# Revit family: RN 90026 Optifitt-Serra-Nippel doppio ridotto
name_source: partatom
category: Rohrformteile
units: mm (PartAtom-declared; Revit-internal decimal feet)

## family parameters
Arbeitsebenenbasiert = Nein
Beim Laden mit Abzugskörper schneiden = Nein
Bemaßung runder Anschluss = Durchmesser verwenden
Gemeinsam genutzt = Nein
Immer vertikal = Ja
Teiletyp = Nicht definiert

## types (14) — shared parameters
1.010.00.2 Blattnummer der Richtlinie = 29
1.010.00.3 Ausgabedatum (Monat) der Richtlinie = 201308
1.010.00.4 Herstellername = R. Nussbaum AG
1.010.00.5 Revisionsdatum der Datei = 20190521
1.010.00.6 Webadresse des Herstellers = http://www.nussbaum.ch
1.100.00.4 Produktbezeichnung = Versorgung
1.110.00.2 Index = 3
1.110.00.4 Produktbezeichnung = Optifitt-Serra
1.960/3L.00.8 Link (URL) = https://www.nussbaum.ch
29.700.00.4 Produktname = Optifitt-Serra-Doppelnippel reduziert
29.700.00.5 Produktkennung = 2
29.700.00.6 Querschnittsform = 1
29.700.00.7 Nennweitensystem = DN
29.700.00.8 Nenndrucksystem = PN
29.710.02.4 Nenndruck = 16
29.710.02.5 max. zul. Überdruck [hPa] = 1600
29.710.02.7 max. zul. Dauer-Betriebsdruck [hPa] = 1600
29.710.02.9 max. zul. Dauer-Betriebstemperatur [°C] = 90
Connector Visibility = Nein
EnclosingSpace Visibility = Nein

## per-type parameters (varying)
- DN=32x20: 1.800.00.3 TGA-Nummer=01900300000000000000000000000000000000000000000016000000000000000025; 1.800.00.4 Kommentarfeld=90026.30, Optifitt-Serra-Doppelnippel reduziert, DN=32x20, L=46, R=1¼; 1.810.00.3 Hersteller-Bestellnummer=90026.30; 1.810.00.4 DATANORM-Nummer=90026.30; 1.810.00.6 GTIN-Nummer=7612945033833; 29.710.02.10 Formstück-Gewicht [kg]=0.172; 29.710.02.3 Benennung=Optifitt-Serra-Doppelnippel reduziert, DN=32x20, L=46, R=1¼; CONNECTOR0_DIAMETER_dX_0r=32 mm; CONNECTOR0_dX_01=19 mm; CONNECTOR0_ref_dX=19 mm; CONNECTOR1_DIAMETER_dX_0r=20 mm; CONNECTOR1_dX_00=31 mm; CONNECTOR1_dX_01=46 mm; CONNECTOR1_ref_dX=31 mm; CONNENCTOR1_ref_dX2=46 mm; R. Nussbaum AG 90026.21 de Visibility=Nein; R. Nussbaum AG 90026.22 de Visibility=Nein; R. Nussbaum AG 90026.23 de Visibility=Nein; R. Nussbaum AG 90026.24 de Visibility=Nein; R. Nussbaum AG 90026.25 de Visibility=Nein; R. Nussbaum AG 90026.26 de Visibility=Nein; R. Nussbaum AG 90026.27 de Visibility=Nein; R. Nussbaum AG 90026.28 de Visibility=Nein; R. Nussbaum AG 90026.29 de Visibility=Nein; R. Nussbaum AG 90026.30 de Visibility=Ja; R. Nussbaum AG 90026.31 de Visibility=Nein; R. Nussbaum AG 90026.32 de Visibility=Nein; R. Nussbaum AG 90026.33 de Visibility=Nein; R. Nussbaum AG 90026.34 de Visibility=Nein
- DN=65x50: 1.800.00.3 TGA-Nummer=01900300000000000000000000000000000000000000000016000000000000000013; 1.800.00.4 Kommentarfeld=90026.34, Optifitt-Serra-Doppelnippel reduziert, DN=65x50, L=70, R=2½; 1.810.00.3 Hersteller-Bestellnummer=90026.34; 1.810.00.4 DATANORM-Nummer=90026.34; 1.810.00.6 GTIN-Nummer=7612945705303; 29.710.02.10 Formstück-Gewicht [kg]=0.631; 29.710.02.3 Benennung=Optifitt-Serra-Doppelnippel reduziert, DN=65x50, L=70, R=2½; CONNECTOR0_DIAMETER_dX_0r=65 mm; CONNECTOR0_dX_01=27 mm; CONNECTOR0_ref_dX=27 mm; CONNECTOR1_DIAMETER_dX_0r=50 mm; CONNECTOR1_dX_00=46 mm; CONNECTOR1_dX_01=70 mm; CONNECTOR1_ref_dX=46 mm; CONNENCTOR1_ref_dX2=70 mm; R. Nussbaum AG 90026.21 de Visibility=Nein; R. Nussbaum AG 90026.22 de Visibility=Nein; R. Nussbaum AG 90026.23 de Visibility=Nein; R. Nussbaum AG 90026.24 de Visibility=Nein; R. Nussbaum AG 90026.25 de Visibility=Nein; R. Nussbaum AG 90026.26 de Visibility=Nein; R. Nussbaum AG 90026.27 de Visibility=Nein; R. Nussbaum AG 90026.28 de Visibility=Nein; R. Nussbaum AG 90026.29 de Visibility=Nein; R. Nussbaum AG 90026.30 de Visibility=Nein; R. Nussbaum AG 90026.31 de Visibility=Nein; R. Nussbaum AG 90026.32 de Visibility=Nein; R. Nussbaum AG 90026.33 de Visibility=Nein; R. Nussbaum AG 90026.34 de Visibility=Ja
- DN=50x40: 1.800.00.3 TGA-Nummer=01900300000000000000000000000000000000000000000016000000000000000012; 1.800.00.4 Kommentarfeld=90026.33, Optifitt-Serra-Doppelnippel reduziert, DN=50x40, L=59, R=2; 1.810.00.3 Hersteller-Bestellnummer=90026.33; 1.810.00.4 DATANORM-Nummer=90026.33; 1.810.00.5 StLB-Nummer=214.557; 1.810.00.6 GTIN-Nummer=7612945033864; 29.710.02.10 Formstück-Gewicht [kg]=0.355; 29.710.02.3 Benennung=Optifitt-Serra-Doppelnippel reduziert, DN=50x40, L=59, R=2; CONNECTOR0_DIAMETER_dX_0r=50 mm; CONNECTOR0_dX_01=24 mm; CONNECTOR0_ref_dX=24 mm; CONNECTOR1_DIAMETER_dX_0r=40 mm; CONNECTOR1_dX_00=40 mm; CONNECTOR1_dX_01=59 mm; CONNECTOR1_ref_dX=40 mm; CONNENCTOR1_ref_dX2=59 mm; Hersteller=R. Nussbaum AG; Modell=90026.33; R. Nussbaum AG 90026.21 de Visibility=Nein; R. Nussbaum AG 90026.22 de Visibility=Nein; R. Nussbaum AG 90026.23 de Visibility=Nein; R. Nussbaum AG 90026.24 de Visibility=Nein; R. Nussbaum AG 90026.25 de Visibility=Nein; R. Nussbaum AG 90026.26 de Visibility=Nein; R. Nussbaum AG 90026.27 de Visibility=Nein; R. Nussbaum AG 90026.28 de Visibility=Nein; R. Nussbaum AG 90026.29 de Visibility=Nein; R. Nussbaum AG 90026.30 de Visibility=Nein; R. Nussbaum AG 90026.31 de Visibility=Nein; R. Nussbaum AG 90026.32 de Visibility=Nein; R. Nussbaum AG 90026.33 de Visibility=Ja; R. Nussbaum AG 90026.34 de Visibility=Nein; Typenkommentare=Optifitt-Serra-Nippel doppio ridotto DN=50x40; URL=https://www.nussbaum.ch
- DN=50x32: 1.800.00.3 TGA-Nummer=01900300000000000000000000000000000000000000000016000000000000000011; 1.800.00.4 Kommentarfeld=90026.32, Optifitt-Serra-Doppelnippel reduziert, DN=50x32, L=59, R=2; 1.810.00.3 Hersteller-Bestellnummer=90026.32; 1.810.00.4 DATANORM-Nummer=90026.32; 1.810.00.6 GTIN-Nummer=7612945033857; 29.710.02.10 Formstück-Gewicht [kg]=0.363; 29.710.02.3 Benennung=Optifitt-Serra-Doppelnippel reduziert, DN=50x32, L=59, R=2; CONNECTOR0_DIAMETER_dX_0r=50 mm; CONNECTOR0_dX_01=24 mm; CONNECTOR0_ref_dX=24 mm; CONNECTOR1_DIAMETER_dX_0r=32 mm; CONNECTOR1_dX_00=39 mm; CONNECTOR1_dX_01=58 mm; CONNECTOR1_ref_dX=39 mm; CONNENCTOR1_ref_dX2=58 mm; Hersteller=R. Nussbaum AG; Modell=90026.32; R. Nussbaum AG 90026.21 de Visibility=Nein; R. Nussbaum AG 90026.22 de Visibility=Nein; R. Nussbaum AG 90026.23 de Visibility=Nein; R. Nussbaum AG 90026.24 de Visibility=Nein; R. Nussbaum AG 90026.25 de Visibility=Nein; R. Nussbaum AG 90026.26 de Visibility=Nein; R. Nussbaum AG 90026.27 de Visibility=Nein; R. Nussbaum AG 90026.28 de Visibility=Nein; R. Nussbaum AG 90026.29 de Visibility=Nein; R. Nussbaum AG 90026.30 de Visibility=Nein; R. Nussbaum AG 90026.31 de Visibility=Nein; R. Nussbaum AG 90026.32 de Visibility=Ja; R. Nussbaum AG 90026.33 de Visibility=Nein; R. Nussbaum AG 90026.34 de Visibility=Nein; Typenkommentare=Optifitt-Serra-Nippel doppio ridotto DN=50x32; URL=https://www.nussbaum.ch
- DN=40x25: 1.800.00.3 TGA-Nummer=01900300000000000000000000000000000000000000000016000000000000000010; 1.800.00.4 Kommentarfeld=90026.31, Optifitt-Serra-Doppelnippel reduziert, DN=40x25, L=52, R=1½; 1.810.00.3 Hersteller-Bestellnummer=90026.31; 1.810.00.4 DATANORM-Nummer=90026.31; 1.810.00.6 GTIN-Nummer=7612945033840; 29.710.02.10 Formstück-Gewicht [kg]=0.226; 29.710.02.3 Benennung=Optifitt-Serra-Doppelnippel reduziert, DN=40x25, L=52, R=1½; CONNECTOR0_DIAMETER_dX_0r=40 mm; CONNECTOR0_dX_01=19 mm; CONNECTOR0_ref_dX=19 mm; CONNECTOR1_DIAMETER_dX_0r=25 mm  [stored 0.082021 ft]; CONNECTOR1_dX_00=35 mm; CONNECTOR1_dX_01=52 mm; CONNECTOR1_ref_dX=35 mm; CONNENCTOR1_ref_dX2=52 mm; Hersteller=R. Nussbaum AG; Modell=90026.31; R. Nussbaum AG 90026.21 de Visibility=Nein; R. Nussbaum AG 90026.22 de Visibility=Nein; R. Nussbaum AG 90026.23 de Visibility=Nein; R. Nussbaum AG 90026.24 de Visibility=Nein; R. Nussbaum AG 90026.25 de Visibility=Nein; R. Nussbaum AG 90026.26 de Visibility=Nein; R. Nussbaum AG 90026.27 de Visibility=Nein; R. Nussbaum AG 90026.28 de Visibility=Nein; R. Nussbaum AG 90026.29 de Visibility=Nein; R. Nussbaum AG 90026.30 de Visibility=Nein; R. Nussbaum AG 90026.31 de Visibility=Ja; R. Nussbaum AG 90026.32 de Visibility=Nein; R. Nussbaum AG 90026.33 de Visibility=Nein; R. Nussbaum AG 90026.34 de Visibility=Nein; Typenkommentare=Optifitt-Serra-Nippel doppio ridotto DN=40x25; URL=https://www.nussbaum.ch
- DN=25x15: 1.800.00.3 TGA-Nummer=01900300000000000000000000000000000000000000000016000000000000000009; 1.800.00.4 Kommentarfeld=90026.29, Optifitt-Serra-Doppelnippel reduziert, DN=25x15, L=40, R=1; 1.810.00.3 Hersteller-Bestellnummer=90026.29; 1.810.00.4 DATANORM-Nummer=90026.29; 1.810.00.6 GTIN-Nummer=7612945033826; 29.710.02.10 Formstück-Gewicht [kg]=0.089; 29.710.02.3 Benennung=Optifitt-Serra-Doppelnippel reduziert, DN=25x15, L=40, R=1; CONNECTOR0_DIAMETER_dX_0r=25 mm  [stored 0.082021 ft]; CONNECTOR0_dX_01=17 mm; CONNECTOR0_ref_dX=17 mm; CONNECTOR1_DIAMETER_dX_0r=15 mm; CONNECTOR1_dX_00=27 mm; CONNECTOR1_dX_01=40 mm; CONNECTOR1_ref_dX=27 mm; CONNENCTOR1_ref_dX2=40 mm; Hersteller=R. Nussbaum AG; Modell=90026.29; R. Nussbaum AG 90026.21 de Visibility=Nein; R. Nussbaum AG 90026.22 de Visibility=Nein; R. Nussbaum AG 90026.23 de Visibility=Nein; R. Nussbaum AG 90026.24 de Visibility=Nein; R. Nussbaum AG 90026.25 de Visibility=Nein; R. Nussbaum AG 90026.26 de Visibility=Nein; R. Nussbaum AG 90026.27 de Visibility=Nein; R. Nussbaum AG 90026.28 de Visibility=Nein; R. Nussbaum AG 90026.29 de Visibility=Ja; R. Nussbaum AG 90026.30 de Visibility=Nein; R. Nussbaum AG 90026.31 de Visibility=Nein; R. Nussbaum AG 90026.32 de Visibility=Nein; R. Nussbaum AG 90026.33 de Visibility=Nein; R. Nussbaum AG 90026.34 de Visibility=Nein; Typenkommentare=Optifitt-Serra-Nippel doppio ridotto DN=25x15; URL=https://www.nussbaum.ch
- DN=20x12: 1.800.00.3 TGA-Nummer=01900300000000000000000000000000000000000000000016000000000000000008; 1.800.00.4 Kommentarfeld=90026.28, Optifitt-Serra-Doppelnippel reduziert, DN=20x12, L=34, R=¾; 1.810.00.3 Hersteller-Bestellnummer=90026.28; 1.810.00.4 DATANORM-Nummer=90026.28; 1.810.00.6 GTIN-Nummer=7612945033819; 29.710.02.10 Formstück-Gewicht [kg]=0.055; 29.710.02.3 Benennung=Optifitt-Serra-Doppelnippel reduziert, DN=20x12, L=34, R=¾; CONNECTOR0_DIAMETER_dX_0r=20 mm; CONNECTOR0_dX_01=15 mm; CONNECTOR0_ref_dX=15 mm; CONNECTOR1_DIAMETER_dX_0r=12 mm  [stored 0.0393701 ft]; CONNECTOR1_dX_00=24 mm; CONNECTOR1_dX_01=34 mm; CONNECTOR1_ref_dX=24 mm; CONNENCTOR1_ref_dX2=34 mm; Hersteller=R. Nussbaum AG; Modell=90026.28; R. Nussbaum AG 90026.21 de Visibility=Nein; R. Nussbaum AG 90026.22 de Visibility=Nein; R. Nussbaum AG 90026.23 de Visibility=Nein; R. Nussbaum AG 90026.24 de Visibility=Nein; R. Nussbaum AG 90026.25 de Visibility=Nein; R. Nussbaum AG 90026.26 de Visibility=Nein; R. Nussbaum AG 90026.27 de Visibility=Nein; R. Nussbaum AG 90026.28 de Visibility=Ja; R. Nussbaum AG 90026.29 de Visibility=Nein; R. Nussbaum AG 90026.30 de Visibility=Nein; R. Nussbaum AG 90026.31 de Visibility=Nein; R. Nussbaum AG 90026.32 de Visibility=Nein; R. Nussbaum AG 90026.33 de Visibility=Nein; R. Nussbaum AG 90026.34 de Visibility=Nein; Typenkommentare=Optifitt-Serra-Nippel doppio ridotto DN=20x12; URL=https://www.nussbaum.ch
- DN=15x10: 1.800.00.3 TGA-Nummer=01900300000000000000000000000000000000000000000016000000000000000007; 1.800.00.4 Kommentarfeld=90026.27, Optifitt-Serra-Doppelnippel reduziert, DN=15x10, L=31, R=½; 1.810.00.3 Hersteller-Bestellnummer=90026.27; 1.810.00.4 DATANORM-Nummer=90026.27; 1.810.00.6 GTIN-Nummer=7612945033802; 29.710.02.10 Formstück-Gewicht [kg]=0.035; 29.710.02.3 Benennung=Optifitt-Serra-Doppelnippel reduziert, DN=15x10, L=31, R=½; CONNECTOR0_DIAMETER_dX_0r=15 mm; CONNECTOR0_dX_01=13 mm; CONNECTOR0_ref_dX=13 mm; CONNECTOR1_DIAMETER_dX_0r=10 mm  [stored 0.0328084 ft]; CONNECTOR1_dX_00=21 mm; CONNECTOR1_dX_01=31 mm; CONNECTOR1_ref_dX=21 mm; CONNENCTOR1_ref_dX2=31 mm; Hersteller=R. Nussbaum AG; Modell=90026.27; R. Nussbaum AG 90026.21 de Visibility=Nein; R. Nussbaum AG 90026.22 de Visibility=Nein; R. Nussbaum AG 90026.23 de Visibility=Nein; R. Nussbaum AG 90026.24 de Visibility=Nein; R. Nussbaum AG 90026.25 de Visibility=Nein; R. Nussbaum AG 90026.26 de Visibility=Nein; R. Nussbaum AG 90026.27 de Visibility=Ja; R. Nussbaum AG 90026.28 de Visibility=Nein; R. Nussbaum AG 90026.29 de Visibility=Nein; R. Nussbaum AG 90026.30 de Visibility=Nein; R. Nussbaum AG 90026.31 de Visibility=Nein; R. Nussbaum AG 90026.32 de Visibility=Nein; R. Nussbaum AG 90026.33 de Visibility=Nein; R. Nussbaum AG 90026.34 de Visibility=Nein; Typenkommentare=Optifitt-Serra-Nippel doppio ridotto DN=15x10; URL=https://www.nussbaum.ch
- DN=40x32: 1.800.00.3 TGA-Nummer=01900300000000000000000000000000000000000000000016000000000000000006; 1.800.00.4 Kommentarfeld=90026.26, Optifitt-Serra-Doppelnippel reduziert, DN=40x32, L=53, R=1½; 1.810.00.3 Hersteller-Bestellnummer=90026.26; 1.810.00.4 DATANORM-Nummer=90026.26; 1.810.00.5 StLB-Nummer=214.556; 1.810.00.6 GTIN-Nummer=7612945033796; 29.710.02.10 Formstück-Gewicht [kg]=0.226; 29.710.02.3 Benennung=Optifitt-Serra-Doppelnippel reduziert, DN=40x32, L=53, R=1½; CONNECTOR0_DIAMETER_dX_0r=40 mm; CONNECTOR0_dX_01=19 mm; CONNECTOR0_ref_dX=19 mm; CONNECTOR1_DIAMETER_dX_0r=32 mm; CONNECTOR1_dX_00=35 mm; CONNECTOR1_dX_01=54 mm; CONNECTOR1_ref_dX=35 mm; CONNENCTOR1_ref_dX2=54 mm; Hersteller=R. Nussbaum AG; Modell=90026.26; R. Nussbaum AG 90026.21 de Visibility=Nein; R. Nussbaum AG 90026.22 de Visibility=Nein; R. Nussbaum AG 90026.23 de Visibility=Nein; R. Nussbaum AG 90026.24 de Visibility=Nein; R. Nussbaum AG 90026.25 de Visibility=Nein; R. Nussbaum AG 90026.26 de Visibility=Ja; R. Nussbaum AG 90026.27 de Visibility=Nein; R. Nussbaum AG 90026.28 de Visibility=Nein; R. Nussbaum AG 90026.29 de Visibility=Nein; R. Nussbaum AG 90026.30 de Visibility=Nein; R. Nussbaum AG 90026.31 de Visibility=Nein; R. Nussbaum AG 90026.32 de Visibility=Nein; R. Nussbaum AG 90026.33 de Visibility=Nein; R. Nussbaum AG 90026.34 de Visibility=Nein; Typenkommentare=Optifitt-Serra-Nippel doppio ridotto DN=40x32; URL=https://www.nussbaum.ch
- DN=32x25: 1.800.00.3 TGA-Nummer=01900300000000000000000000000000000000000000000016000000000000000005; 1.800.00.4 Kommentarfeld=90026.25, Optifitt-Serra-Doppelnippel reduziert, DN=32x25, L=49, R=1¼; 1.810.00.3 Hersteller-Bestellnummer=90026.25; 1.810.00.4 DATANORM-Nummer=90026.25; 1.810.00.5 StLB-Nummer=214.555; 1.810.00.6 GTIN-Nummer=7612945033789; 29.710.02.10 Formstück-Gewicht [kg]=0.161; 29.710.02.3 Benennung=Optifitt-Serra-Doppelnippel reduziert, DN=32x25, L=49, R=1¼; CONNECTOR0_DIAMETER_dX_0r=32 mm; CONNECTOR0_dX_01=19 mm; CONNECTOR0_ref_dX=19 mm; CONNECTOR1_DIAMETER_dX_0r=25 mm  [stored 0.082021 ft]; CONNECTOR1_dX_00=32 mm; CONNECTOR1_dX_01=49 mm; CONNECTOR1_ref_dX=32 mm; CONNENCTOR1_ref_dX2=49 mm; R. Nussbaum AG 90026.21 de Visibility=Nein; R. Nussbaum AG 90026.22 de Visibility=Nein; R. Nussbaum AG 90026.23 de Visibility=Nein; R. Nussbaum AG 90026.24 de Visibility=Nein; R. Nussbaum AG 90026.25 de Visibility=Ja; R. Nussbaum AG 90026.26 de Visibility=Nein; R. Nussbaum AG 90026.27 de Visibility=Nein; R. Nussbaum AG 90026.28 de Visibility=Nein; R. Nussbaum AG 90026.29 de Visibility=Nein; R. Nussbaum AG 90026.30 de Visibility=Nein; R. Nussbaum AG 90026.31 de Visibility=Nein; R. Nussbaum AG 90026.32 de Visibility=Nein; R. Nussbaum AG 90026.33 de Visibility=Nein; R. Nussbaum AG 90026.34 de Visibility=Nein
- DN=25x20: 1.800.00.3 TGA-Nummer=01900300000000000000000000000000000000000000000016000000000000000004; 1.800.00.4 Kommentarfeld=90026.24, Optifitt-Serra-Doppelnippel reduziert, DN=25x20, L=42, R=1; 1.810.00.3 Hersteller-Bestellnummer=90026.24; 1.810.00.4 DATANORM-Nummer=90026.24; 1.810.00.5 StLB-Nummer=214.554; 1.810.00.6 GTIN-Nummer=7612945033772; 29.710.02.10 Formstück-Gewicht [kg]=0.094; 29.710.02.3 Benennung=Optifitt-Serra-Doppelnippel reduziert, DN=25x20, L=42, R=1; CONNECTOR0_DIAMETER_dX_0r=25 mm  [stored 0.082021 ft]; CONNECTOR0_dX_01=17 mm; CONNECTOR0_ref_dX=17 mm; CONNECTOR1_DIAMETER_dX_0r=20 mm; CONNECTOR1_dX_00=27 mm; CONNECTOR1_dX_01=42 mm; CONNECTOR1_ref_dX=27 mm; CONNENCTOR1_ref_dX2=42 mm; Hersteller=R. Nussbaum AG; Modell=90026.24; R. Nussbaum AG 90026.21 de Visibility=Nein; R. Nussbaum AG 90026.22 de Visibility=Nein; R. Nussbaum AG 90026.23 de Visibility=Nein; R. Nussbaum AG 90026.24 de Visibility=Ja; R. Nussbaum AG 90026.25 de Visibility=Nein; R. Nussbaum AG 90026.26 de Visibility=Nein; R. Nussbaum AG 90026.27 de Visibility=Nein; R. Nussbaum AG 90026.28 de Visibility=Nein; R. Nussbaum AG 90026.29 de Visibility=Nein; R. Nussbaum AG 90026.30 de Visibility=Nein; R. Nussbaum AG 90026.31 de Visibility=Nein; R. Nussbaum AG 90026.32 de Visibility=Nein; R. Nussbaum AG 90026.33 de Visibility=Nein; R. Nussbaum AG 90026.34 de Visibility=Nein; Typenkommentare=Optifitt-Serra-Nippel doppio ridotto DN=25x20; URL=https://www.nussbaum.ch
- DN=20x15: 1.800.00.3 TGA-Nummer=01900300000000000000000000000000000000000000000016000000000000000003; 1.800.00.4 Kommentarfeld=90026.23, Optifitt-Serra-Doppelnippel reduziert, DN=20x15, L=37, R=¾; 1.810.00.3 Hersteller-Bestellnummer=90026.23; 1.810.00.4 DATANORM-Nummer=90026.23; 1.810.00.5 StLB-Nummer=214.553; 1.810.00.6 GTIN-Nummer=7612945033765; 29.710.02.10 Formstück-Gewicht [kg]=0.063; 29.710.02.3 Benennung=Optifitt-Serra-Doppelnippel reduziert, DN=20x15, L=37, R=¾; CONNECTOR0_DIAMETER_dX_0r=20 mm; CONNECTOR0_dX_01=15 mm; CONNECTOR0_ref_dX=15 mm; CONNECTOR1_DIAMETER_dX_0r=15 mm; CONNECTOR1_dX_00=24 mm; CONNECTOR1_dX_01=37 mm; CONNECTOR1_ref_dX=24 mm; CONNENCTOR1_ref_dX2=37 mm; Hersteller=R. Nussbaum AG; Modell=90026.23; R. Nussbaum AG 90026.21 de Visibility=Nein; R. Nussbaum AG 90026.22 de Visibility=Nein; R. Nussbaum AG 90026.23 de Visibility=Ja; R. Nussbaum AG 90026.24 de Visibility=Nein; R. Nussbaum AG 90026.25 de Visibility=Nein; R. Nussbaum AG 90026.26 de Visibility=Nein; R. Nussbaum AG 90026.27 de Visibility=Nein; R. Nussbaum AG 90026.28 de Visibility=Nein; R. Nussbaum AG 90026.29 de Visibility=Nein; R. Nussbaum AG 90026.30 de Visibility=Nein; R. Nussbaum AG 90026.31 de Visibility=Nein; R. Nussbaum AG 90026.32 de Visibility=Nein; R. Nussbaum AG 90026.33 de Visibility=Nein; R. Nussbaum AG 90026.34 de Visibility=Nein; Typenkommentare=Optifitt-Serra-Nippel doppio ridotto DN=20x15; URL=https://www.nussbaum.ch
- DN=15x12: 1.800.00.3 TGA-Nummer=01900300000000000000000000000000000000000000000016000000000000000002; 1.800.00.4 Kommentarfeld=90026.22, Optifitt-Serra-Doppelnippel reduziert, DN=15x12, L=32, R=½; 1.810.00.3 Hersteller-Bestellnummer=90026.22; 1.810.00.4 DATANORM-Nummer=90026.22; 1.810.00.5 StLB-Nummer=214.552; 1.810.00.6 GTIN-Nummer=7612945033758; 29.710.02.10 Formstück-Gewicht [kg]=0.039; 29.710.02.3 Benennung=Optifitt-Serra-Doppelnippel reduziert, DN=15x12, L=32, R=½; CONNECTOR0_DIAMETER_dX_0r=15 mm; CONNECTOR0_dX_01=13 mm; CONNECTOR0_ref_dX=13 mm; CONNECTOR1_DIAMETER_dX_0r=12 mm  [stored 0.0393701 ft]; CONNECTOR1_dX_00=22 mm; CONNECTOR1_dX_01=32 mm; CONNECTOR1_ref_dX=22 mm; CONNENCTOR1_ref_dX2=32 mm; Hersteller=R. Nussbaum AG; Modell=90026.22; R. Nussbaum AG 90026.21 de Visibility=Nein; R. Nussbaum AG 90026.22 de Visibility=Ja; R. Nussbaum AG 90026.23 de Visibility=Nein; R. Nussbaum AG 90026.24 de Visibility=Nein; R. Nussbaum AG 90026.25 de Visibility=Nein; R. Nussbaum AG 90026.26 de Visibility=Nein; R. Nussbaum AG 90026.27 de Visibility=Nein; R. Nussbaum AG 90026.28 de Visibility=Nein; R. Nussbaum AG 90026.29 de Visibility=Nein; R. Nussbaum AG 90026.30 de Visibility=Nein; R. Nussbaum AG 90026.31 de Visibility=Nein; R. Nussbaum AG 90026.32 de Visibility=Nein; R. Nussbaum AG 90026.33 de Visibility=Nein; R. Nussbaum AG 90026.34 de Visibility=Nein; Typenkommentare=Optifitt-Serra-Nippel doppio ridotto DN=15x12; URL=https://www.nussbaum.ch
- DN=12x10: 1.800.00.3 TGA-Nummer=01900300000000000000000000000000000000000000000016000000000000000001; 1.800.00.4 Kommentarfeld=90026.21, Optifitt-Serra-Doppelnippel reduziert, DN=12x10, L=28, R=3/8; 1.810.00.3 Hersteller-Bestellnummer=90026.21; 1.810.00.4 DATANORM-Nummer=90026.21; 1.810.00.5 StLB-Nummer=214.551; 1.810.00.6 GTIN-Nummer=7612945033741; 29.710.02.10 Formstück-Gewicht [kg]=0.025; 29.710.02.3 Benennung=Optifitt-Serra-Doppelnippel reduziert, DN=12x10, L=28, R=3/8; CONNECTOR0_DIAMETER_dX_0r=12 mm  [stored 0.0393701 ft]; CONNECTOR0_dX_01=10 mm  [stored 0.0328084 ft]; CONNECTOR0_ref_dX=10 mm  [stored 0.0328084 ft]; CONNECTOR1_DIAMETER_dX_0r=10 mm  [stored 0.0328084 ft]; CONNECTOR1_dX_00=18 mm; CONNECTOR1_dX_01=28 mm; CONNECTOR1_ref_dX=18 mm; CONNENCTOR1_ref_dX2=28 mm; Hersteller=R. Nussbaum AG; Modell=90026.21; R. Nussbaum AG 90026.21 de Visibility=Ja; R. Nussbaum AG 90026.22 de Visibility=Nein; R. Nussbaum AG 90026.23 de Visibility=Nein; R. Nussbaum AG 90026.24 de Visibility=Nein; R. Nussbaum AG 90026.25 de Visibility=Nein; R. Nussbaum AG 90026.26 de Visibility=Nein; R. Nussbaum AG 90026.27 de Visibility=Nein; R. Nussbaum AG 90026.28 de Visibility=Nein; R. Nussbaum AG 90026.29 de Visibility=Nein; R. Nussbaum AG 90026.30 de Visibility=Nein; R. Nussbaum AG 90026.31 de Visibility=Nein; R. Nussbaum AG 90026.32 de Visibility=Nein; R. Nussbaum AG 90026.33 de Visibility=Nein; R. Nussbaum AG 90026.34 de Visibility=Nein; Typenkommentare=Optifitt-Serra-Nippel doppio ridotto DN=12x10; URL=https://www.nussbaum.ch

note: [stored X ft] marks values corroborated as IEEE doubles in the binary element streams (Revit-internal decimal feet)
